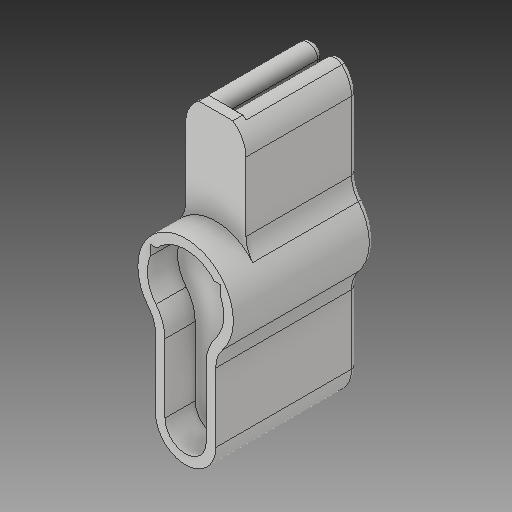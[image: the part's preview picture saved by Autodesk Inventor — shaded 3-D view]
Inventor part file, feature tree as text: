
AUTODESK INVENTOR PART (.ipt)
format: ipt  version: 2019 (Build 230136000, 136)  size: 242,688 bytes
history: native  units: mm
features: sketch x6, other x3
ambient origin geometry x8: Origin, YZ Plane, XZ Plane, XY Plane, X Axis, Y Axis, Z Axis, Center Point
bodies: Solid1 (feature_tree)
feature tree (9):
  other  "sample_hold_v2.ipt"
  other  "Solid1::sample_hold_v2.ipt"
  other  "TaggingFeature1"
  sketch  "Sketch1"  dims[d0=10.0mm]
  sketch  "Sketch2"
  sketch  "Sketch4"
  sketch  "Sketch5"
  sketch  "Sketch6"
  sketch  "Sketch7"
